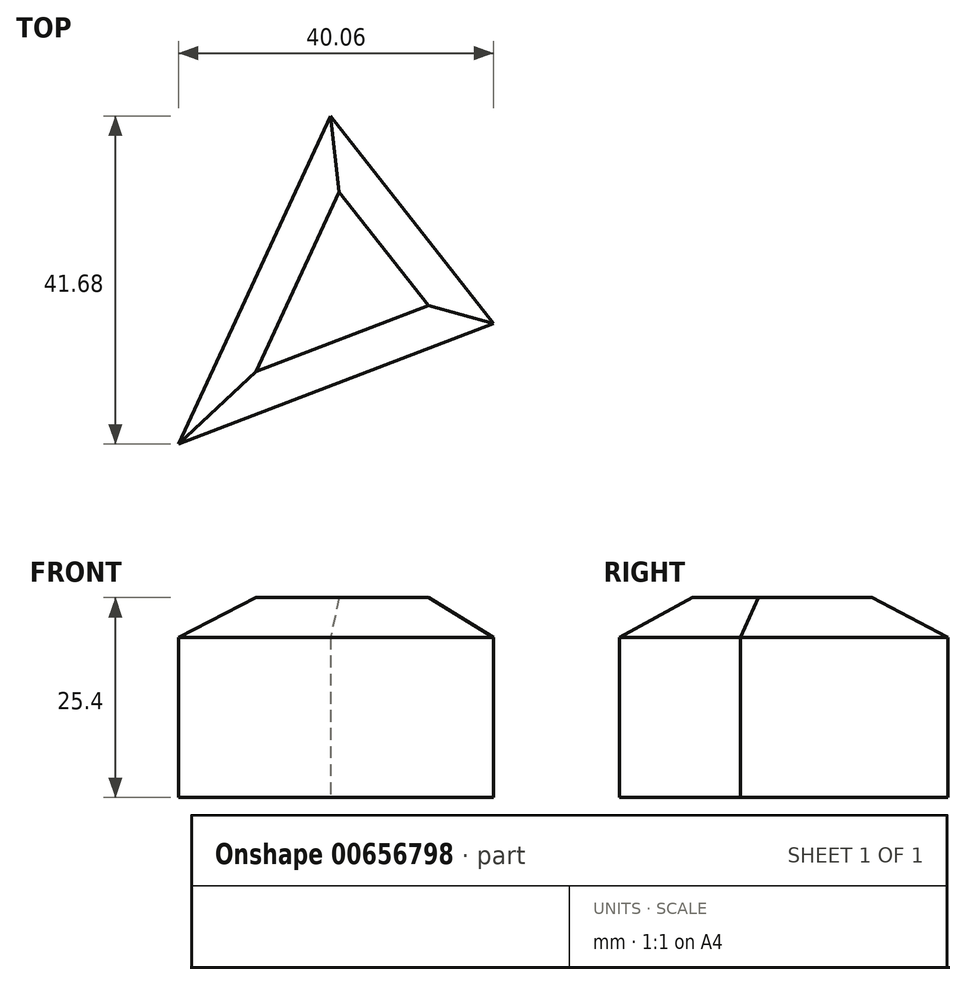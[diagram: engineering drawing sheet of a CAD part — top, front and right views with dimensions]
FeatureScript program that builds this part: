
annotation { "Feature Type Name" : "Feature", "Feature Type Description" : "" }
export const myFeature = defineFeature(function(context is Context, id is Id, definition is map)
    precondition{}
    {
        {
            var Q0;
            Q0=qCreatedBy(makeId("Top.planeOp"),FACE);
            var sketch = newSketch(context, id + "F0", { "sketchPlane" : qUnion([Q0])});
            skLineSegment(sketch, "E0", {"start": v(34.65, 65.32) * mm, "end": v(15.34, 23.64) * mm});
            skLineSegment(sketch, "E1", {"start": v(15.34, 23.64) * mm, "end": v(55.4, 38.98) * mm});
            skLineSegment(sketch, "E2", {"start": v(55.4, 38.98) * mm, "end": v(34.65, 65.32) * mm});
            skSolve(sketch);
        }
        {
            var Q0;
            Q0=makeQuery(id+"F0.imprint","IMPRINT",FACE,{"disambiguationData":[TD([[makeQuery(id+"F0.imprint","IMPRINT",EDGE,{"derivedFrom":sQuery(id+"F0.wireOp",EDGE,"E0")}),1.0]])]});
            var sketch = newSketch(context, id + "F1", { "sketchPlane" : qUnion([Q0])});
            skSolve(sketch);
        }
        {
            var Q0;
            Q0=makeQuery(id+"F1.imprint","IMPRINT",FACE,{"disambiguationData":[TD([[makeQuery(id+"F1.imprint","IMPRINT",EDGE,{"derivedFrom":makeQuery(id+"F0.imprint","IMPRINT",EDGE,{"derivedFrom":sQuery(id+"F0.wireOp",EDGE,"E0")})}),1.0]])]});
            extrude(context, id + "F2", {"entities" : qUnion([Q0]), "depth" : 25.4 * mm, "offsetDistance" : 25.4 * mm});
        }
        {
            var Q0;
            Q0=makeQuery(id+"F2.opExtrude","CAP_EDGE",EDGE,{"disambiguationData":[OSD([sQuery(id+"F0.wireOp",EDGE,"E2")])],"isStart":false});
            var Q1;
            Q1=makeQuery(id+"F2.opExtrude","CAP_EDGE",EDGE,{"disambiguationData":[OSD([sQuery(id+"F0.wireOp",EDGE,"E0")])],"isStart":false});
            var Q2;
            Q2=makeQuery(id+"F2.opExtrude","CAP_EDGE",EDGE,{"disambiguationData":[OSD([sQuery(id+"F0.wireOp",EDGE,"E1")])],"isStart":false});
            chamfer(context, id + "F3", {"entities" : qUnion([Q0, Q1, Q2]), "width" : 5.08 * mm, "tangentPropagation" : true});
        }
    });
